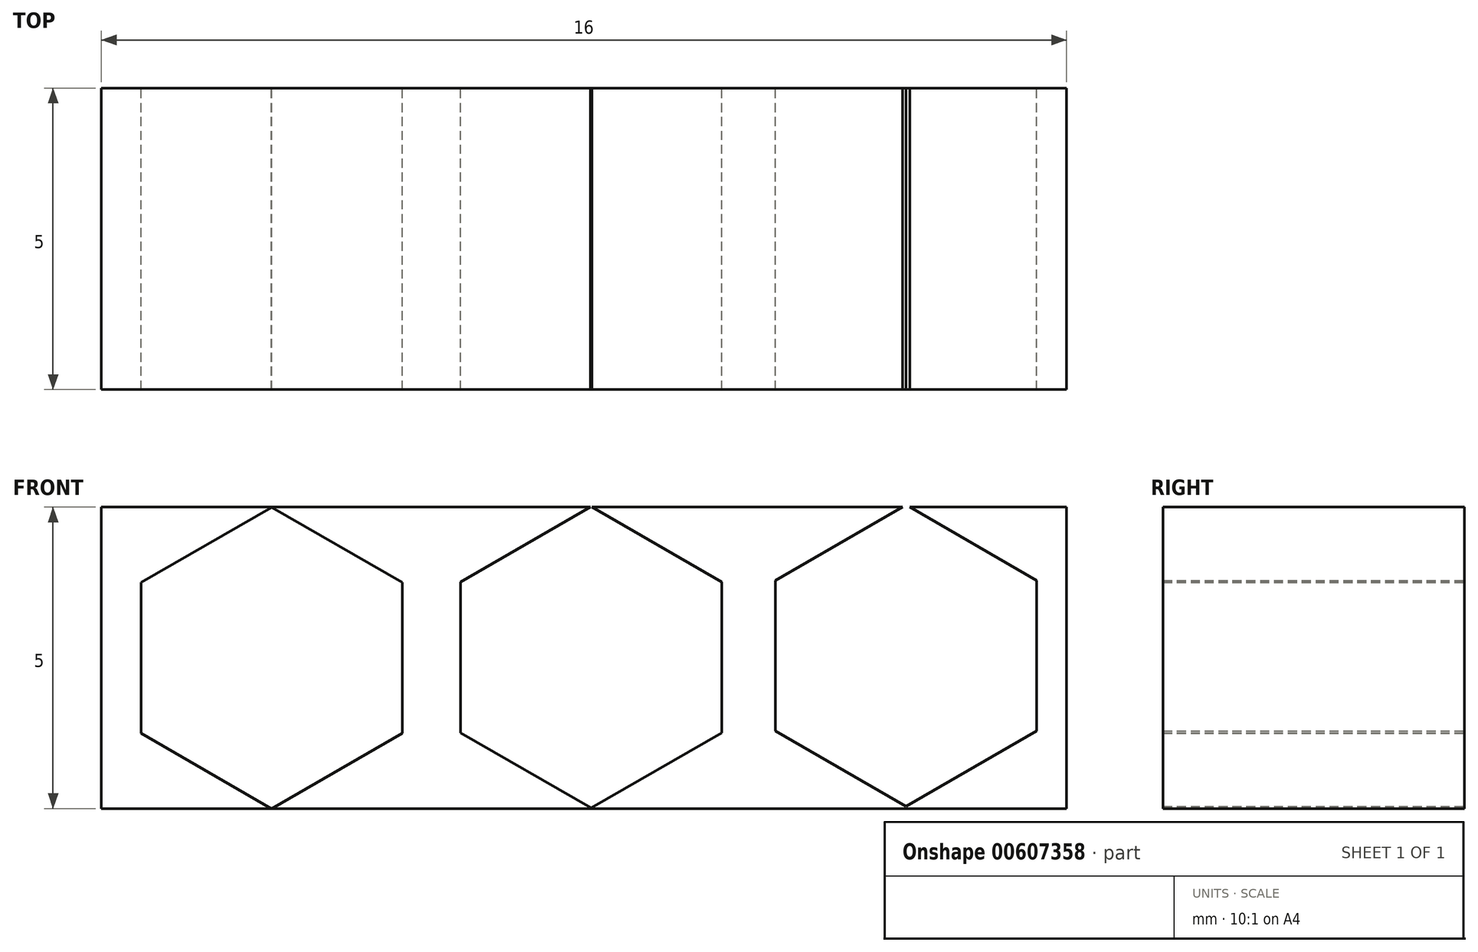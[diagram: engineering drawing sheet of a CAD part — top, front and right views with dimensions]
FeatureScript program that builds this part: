
annotation { "Feature Type Name" : "Feature", "Feature Type Description" : "" }
export const myFeature = defineFeature(function(context is Context, id is Id, definition is map)
    precondition{}
    {
        {
            var Q0;
            Q0=qCreatedBy(makeId("Front.planeOp"),FACE);
            var sketch = newSketch(context, id + "F0", { "sketchPlane" : qUnion([Q0])});
            skLineSegment(sketch, "E0.bottom", {"start": v(0, 0) * mm, "end": v(16, 0) * mm});
            skLineSegment(sketch, "E0.top", {"start": v(0, 5) * mm, "end": v(16, 5) * mm});
            skLineSegment(sketch, "E0.left", {"start": v(0, 0) * mm, "end": v(0, 5) * mm});
            skLineSegment(sketch, "E0.right", {"start": v(16, 0) * mm, "end": v(16, 5) * mm});
            skCircle(sketch, "E1.cCircle", {"center": v(2.82, 2.5) * mm, "radius": 2.17 * mm, "construction": true});
            skLineSegment(sketch, "E1.0", {"start": v(4.99, 3.75) * mm, "end": v(4.99, 1.25) * mm});
            skLineSegment(sketch, "E1.1", {"start": v(4.99, 1.25) * mm, "end": v(2.82, 0) * mm});
            skLineSegment(sketch, "E1.2", {"start": v(2.82, 0) * mm, "end": v(0.66, 1.25) * mm});
            skLineSegment(sketch, "E1.3", {"start": v(0.66, 1.25) * mm, "end": v(0.66, 3.75) * mm});
            skLineSegment(sketch, "E1.4", {"start": v(0.66, 3.75) * mm, "end": v(2.82, 5) * mm});
            skLineSegment(sketch, "E1.5", {"start": v(2.82, 5) * mm, "end": v(4.99, 3.75) * mm});
            skPoint(sketch, "E1.0.midPoint", {"position": v(4.99, 2.5) * mm});
            skPoint(sketch, "E2.cCircle.perimeterSnap0", {"position": v(3.9, 4.37) * mm});
            skPoint(sketch, "E2.0.midPoint.positionSnap0", {"position": v(3.9, 4.37) * mm});
            skCircle(sketch, "E3.cCircle", {"center": v(8.12, 2.5) * mm, "radius": 2.17 * mm, "construction": true});
            skLineSegment(sketch, "E3.0", {"start": v(10.28, 3.76) * mm, "end": v(10.28, 1.26) * mm});
            skLineSegment(sketch, "E3.1", {"start": v(10.28, 1.26) * mm, "end": v(8.12, 0) * mm});
            skLineSegment(sketch, "E3.2", {"start": v(8.12, 0) * mm, "end": v(5.95, 1.26) * mm});
            skLineSegment(sketch, "E3.3", {"start": v(5.95, 1.26) * mm, "end": v(5.95, 3.76) * mm});
            skLineSegment(sketch, "E3.4", {"start": v(5.95, 3.76) * mm, "end": v(8.12, 5) * mm});
            skLineSegment(sketch, "E3.5", {"start": v(8.12, 5) * mm, "end": v(10.28, 3.76) * mm});
            skPoint(sketch, "E3.0.midPoint", {"position": v(10.28, 2.5) * mm});
            skCircle(sketch, "E4.cCircle", {"center": v(8.12, 2.5) * mm, "radius": 1.19 * mm, "construction": true});
            skLineSegment(sketch, "E4.0", {"start": v(9.3, 2.9) * mm, "end": v(9.3, 2.12) * mm, "construction": true});
            skLineSegment(sketch, "E4.1", {"start": v(9.3, 2.12) * mm, "end": v(8.85, 1.5) * mm, "construction": true});
            skLineSegment(sketch, "E4.2", {"start": v(8.85, 1.5) * mm, "end": v(8.12, 1.26) * mm, "construction": true});
            skLineSegment(sketch, "E4.3", {"start": v(8.12, 1.26) * mm, "end": v(7.38, 1.5) * mm, "construction": true});
            skLineSegment(sketch, "E4.4", {"start": v(7.38, 1.5) * mm, "end": v(6.93, 2.12) * mm, "construction": true});
            skLineSegment(sketch, "E4.5", {"start": v(6.93, 2.12) * mm, "end": v(6.93, 2.9) * mm, "construction": true});
            skLineSegment(sketch, "E4.6", {"start": v(6.93, 2.9) * mm, "end": v(7.38, 3.52) * mm, "construction": true});
            skLineSegment(sketch, "E4.7", {"start": v(7.38, 3.52) * mm, "end": v(8.12, 3.76) * mm, "construction": true});
            skLineSegment(sketch, "E4.8", {"start": v(8.12, 3.76) * mm, "end": v(8.85, 3.52) * mm, "construction": true});
            skLineSegment(sketch, "E4.9", {"start": v(8.85, 3.52) * mm, "end": v(9.3, 2.9) * mm, "construction": true});
            skPoint(sketch, "E4.0.midPoint", {"position": v(9.3, 2.5) * mm});
            skCircle(sketch, "E5.cCircle", {"center": v(2.82, 2.5) * mm, "radius": 1.2 * mm, "construction": true});
            skLineSegment(sketch, "E5.0", {"start": v(3.46, 3.58) * mm, "end": v(3.97, 3) * mm});
            skLineSegment(sketch, "E5.1", {"start": v(3.97, 3) * mm, "end": v(4.05, 2.23) * mm});
            skLineSegment(sketch, "E5.2", {"start": v(4.05, 2.23) * mm, "end": v(3.65, 1.56) * mm});
            skLineSegment(sketch, "E5.3", {"start": v(3.65, 1.56) * mm, "end": v(2.94, 1.25) * mm});
            skLineSegment(sketch, "E5.4", {"start": v(2.94, 1.25) * mm, "end": v(2.18, 1.42) * mm});
            skLineSegment(sketch, "E5.5", {"start": v(2.18, 1.42) * mm, "end": v(1.67, 2) * mm});
            skLineSegment(sketch, "E5.6", {"start": v(1.67, 2) * mm, "end": v(1.6, 2.77) * mm});
            skLineSegment(sketch, "E5.7", {"start": v(1.6, 2.77) * mm, "end": v(1.99, 3.44) * mm});
            skLineSegment(sketch, "E5.8", {"start": v(1.99, 3.44) * mm, "end": v(2.7, 3.75) * mm});
            skLineSegment(sketch, "E5.9", {"start": v(2.7, 3.75) * mm, "end": v(3.46, 3.58) * mm});
            skPoint(sketch, "E5.0.midPoint", {"position": v(3.72, 3.29) * mm});
            skCircle(sketch, "E6.cCircle", {"center": v(13.34, 2.53) * mm, "radius": 2.17 * mm, "construction": true});
            skLineSegment(sketch, "E6.0", {"start": v(13.34, 5.03) * mm, "end": v(15.5, 3.78) * mm});
            skLineSegment(sketch, "E6.1", {"start": v(15.5, 3.78) * mm, "end": v(15.5, 1.28) * mm});
            skLineSegment(sketch, "E6.2", {"start": v(15.5, 1.28) * mm, "end": v(13.34, 0.03) * mm});
            skLineSegment(sketch, "E6.3", {"start": v(13.34, 0.03) * mm, "end": v(11.18, 1.28) * mm});
            skLineSegment(sketch, "E6.4", {"start": v(11.18, 1.28) * mm, "end": v(11.18, 3.78) * mm});
            skLineSegment(sketch, "E6.5", {"start": v(11.18, 3.78) * mm, "end": v(13.34, 5.03) * mm});
            skPoint(sketch, "E6.0.midPoint", {"position": v(14.42, 4.4) * mm});
            skCircle(sketch, "E7.cCircle", {"center": v(13.34, 2.53) * mm, "radius": 1.21 * mm, "construction": true});
            skLineSegment(sketch, "E7.0", {"start": v(13.58, 3.78) * mm, "end": v(14.27, 3.4) * mm});
            skLineSegment(sketch, "E7.1", {"start": v(14.27, 3.4) * mm, "end": v(14.6, 2.7) * mm});
            skLineSegment(sketch, "E7.2", {"start": v(14.6, 2.7) * mm, "end": v(14.46, 1.92) * mm});
            skLineSegment(sketch, "E7.3", {"start": v(14.46, 1.92) * mm, "end": v(13.88, 1.38) * mm});
            skLineSegment(sketch, "E7.4", {"start": v(13.88, 1.38) * mm, "end": v(13.1, 1.28) * mm});
            skLineSegment(sketch, "E7.5", {"start": v(13.1, 1.28) * mm, "end": v(12.41, 1.66) * mm});
            skLineSegment(sketch, "E7.6", {"start": v(12.41, 1.66) * mm, "end": v(12.08, 2.38) * mm});
            skLineSegment(sketch, "E7.7", {"start": v(12.08, 2.38) * mm, "end": v(12.23, 3.15) * mm});
            skLineSegment(sketch, "E7.8", {"start": v(12.23, 3.15) * mm, "end": v(12.8, 3.69) * mm});
            skLineSegment(sketch, "E7.9", {"start": v(12.8, 3.69) * mm, "end": v(13.58, 3.78) * mm});
            skPoint(sketch, "E7.0.midPoint", {"position": v(13.93, 3.6) * mm});
            skSolve(sketch);
        }
        {
            var Q0;
            {var subQ7=sQuery(id+"F0.wireOp",EDGE,"E0.left");Q0=makeQuery(id+"F0.imprint","IMPRINT",FACE,{"disambiguationData":[TD([[makeQuery(id+"F0.imprint","IMPRINT",EDGE,{"derivedFrom":subQ7}),-1.0]])]});}
            extrude(context, id + "F1", {"entities" : qUnion([Q0]), "depth" : 5 * mm, "offsetDistance" : 25 * mm});
        }
    });
